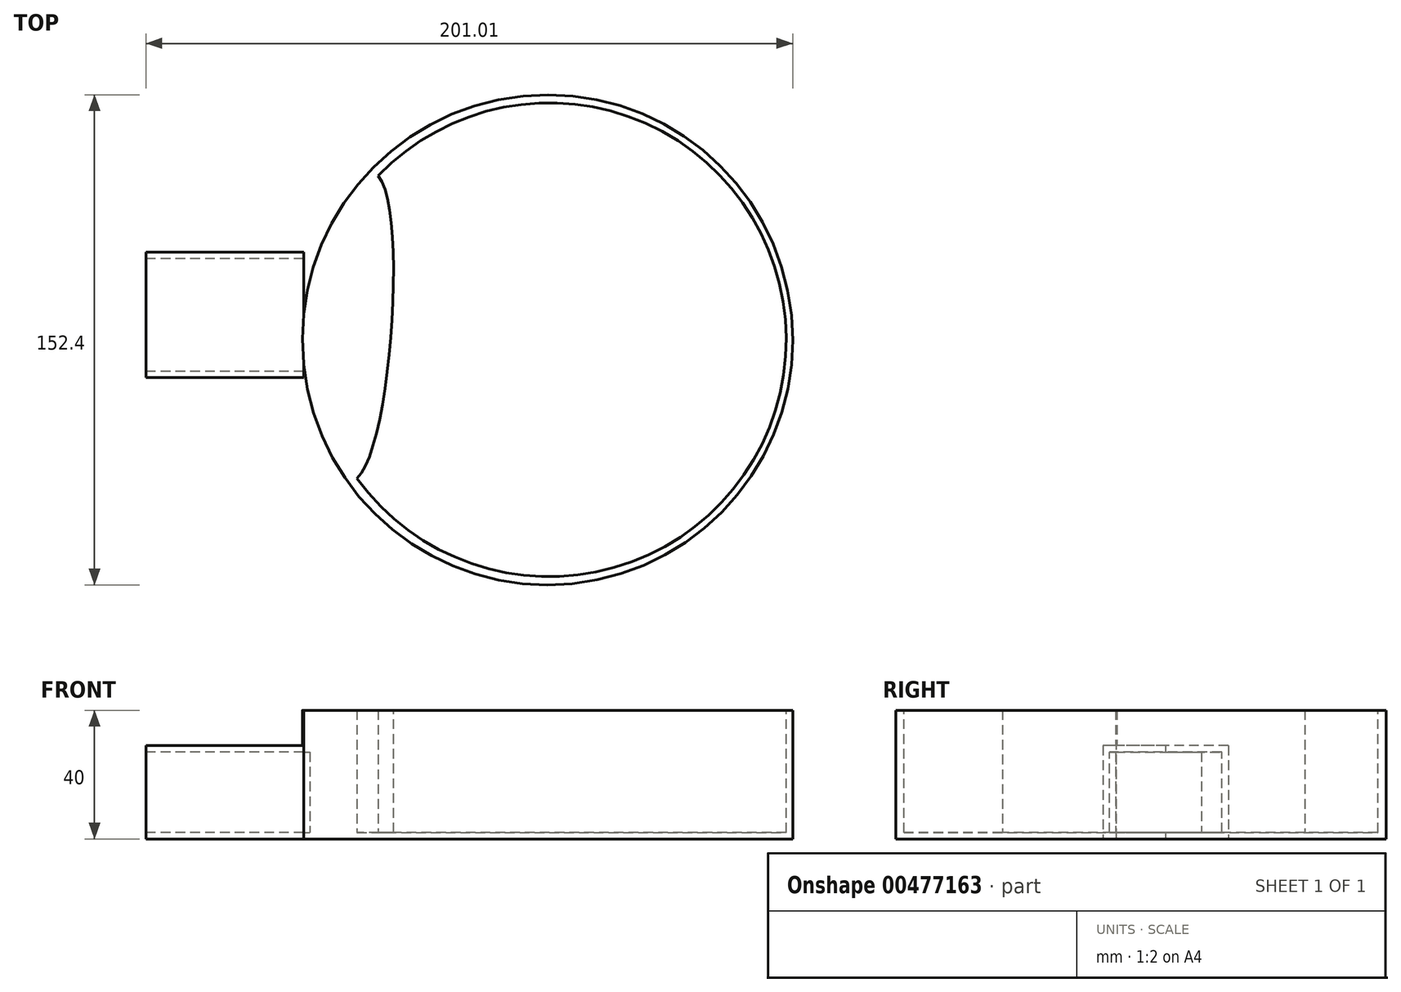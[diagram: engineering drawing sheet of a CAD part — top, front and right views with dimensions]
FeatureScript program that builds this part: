
annotation { "Feature Type Name" : "Feature", "Feature Type Description" : "" }
export const myFeature = defineFeature(function(context is Context, id is Id, definition is map)
    precondition{}
    {
        {
            var Q0;
            Q0=qCreatedBy(makeId("Top.planeOp"),FACE);
            var sketch = newSketch(context, id + "F0", { "sketchPlane" : qUnion([Q0])});
            skLineSegment(sketch, "E0.bottom", {"start": v(-74.8, 22.12) * mm, "end": v(-25.8, 22.12) * mm});
            skLineSegment(sketch, "E0.top", {"start": v(-74.8, -16.88) * mm, "end": v(-25.8, -16.88) * mm});
            skLineSegment(sketch, "E0.left", {"start": v(-74.8, 22.12) * mm, "end": v(-74.8, -16.88) * mm});
            skLineSegment(sketch, "E0.right", {"start": v(-25.8, 22.12) * mm, "end": v(-25.8, -16.88) * mm});
            skPoint(sketch, "E1.firstSnap0", {"position": v(-74.8, 2.62) * mm});
            skPoint(sketch, "E1.oppositeSnap0", {"position": v(-74.8, 2.62) * mm});
            skSolve(sketch);
        }
        {
            var Q0;
            Q0=makeQuery(id+"F0.imprint","IMPRINT",FACE,{"disambiguationData":[TD([[makeQuery(id+"F0.imprint","IMPRINT",EDGE,{"derivedFrom":sQuery(id+"F0.wireOp",EDGE,"E0.bottom")}),-1.0]])]});
            extrude(context, id + "F1", {"entities" : qUnion([Q0]), "depth" : 29 * mm});
        }
        {
            var Q0;
            Q0=makeQuery(id+"F1.opExtrude","SWEPT_FACE",FACE,{"disambiguationData":[OSD([sQuery(id+"F0.wireOp",EDGE,"E0.left")])]});
            var sketch = newSketch(context, id + "F2", { "sketchPlane" : qUnion([Q0])});
            skLineSegment(sketch, "E2.bottom", {"start": v(-20.12, 27) * mm, "end": v(14.88, 27) * mm});
            skLineSegment(sketch, "E2.top", {"start": v(-20.12, 2) * mm, "end": v(14.88, 2) * mm});
            skLineSegment(sketch, "E2.left", {"start": v(-20.12, 27) * mm, "end": v(-20.12, 2) * mm});
            skLineSegment(sketch, "E2.right", {"start": v(14.88, 27) * mm, "end": v(14.88, 2) * mm});
            skSolve(sketch);
        }
        {
            var Q0;
            Q0=qCreatedBy(makeId("Top.planeOp"),FACE);
            var sketch = newSketch(context, id + "F3", { "sketchPlane" : qUnion([Q0])});
            skCircle(sketch, "E3", {"center": v(50.02, -5.1) * mm, "radius": 76.2 * mm});
            skSolve(sketch);
        }
        {
            var Q0;
            Q0 = qSketchRegion(id + "F3", true);
            extrude(context, id + "F4", {"entities" : qUnion([Q0]), "operationType" : NewBodyOperationType.ADD, "depth" : 40 * mm});
        }
        {
            var Q0;
            Q0=makeQuery(id+"F4.opExtrude","CAP_FACE",FACE,{"disambiguationData":[OSD([sQuery(id+"F3.wireOp",EDGE,"E3")])],"isStart":false});
            var sketch = newSketch(context, id + "F5", { "sketchPlane" : qUnion([Q0])});
            skCircle(sketch, "E4", {"center": v(50.56, -5.1) * mm, "radius": 73.66 * mm});
            skSolve(sketch);
        }
        {
            var Q0;
            Q0 = qSketchRegion(id + "F5", true);
            extrude(context, id + "F6", {"entities" : qUnion([Q0]), "operationType" : NewBodyOperationType.REMOVE, "oppositeDirection" : true, "depth" : 38 * mm});
        }
        {
            var Q0;
            Q0=makeQuery(id+"F2.imprint","IMPRINT",FACE,{"disambiguationData":[TD([[makeQuery(id+"F2.imprint","IMPRINT",EDGE,{"derivedFrom":sQuery(id+"F2.wireOp",EDGE,"E2.bottom")}),-1.0]])]});
            extrude(context, id + "F7", {"entities" : qUnion([Q0]), "operationType" : NewBodyOperationType.REMOVE, "oppositeDirection" : true, "depth" : 147.5 * mm});
        }
        {
            var Q0;
            Q0=makeQuery(id+"F7.boolean.opBoolean","MERGE",FACE,{"derivedFrom":[makeQuery(id+"F6.boolean.opBoolean","COPY",FACE,{"derivedFrom":makeQuery(id+"F6.opExtrude","CAP_FACE",FACE,{"disambiguationData":[OSD([sQuery(id+"F5.wireOp",EDGE,"E4")])],"isStart":false})}),makeQuery(id+"F7.opExtrude","SWEPT_FACE",FACE,{"disambiguationData":[OSD([sQuery(id+"F2.wireOp",EDGE,"E2.top")])]})]});
            var sketch = newSketch(context, id + "F8", { "sketchPlane" : qUnion([Q0])});
            skFitSpline(sketch, "E5", {"points": [v(-9.2, -48.15) * mm, v(-25.8, 0) * mm, v(-2.58, 45.92) * mm, v(-9.2, -48.15) * mm]});
            skSolve(sketch);
        }
        {
            var Q0;
            {var subQ2=sQuery(id+"F2.wireOp",EDGE,"E2.top");var subQ3=makeQuery(id+"F7.opExtrude","SWEPT_FACE",FACE,{"disambiguationData":[OSD([subQ2])]});var subQ5=sQuery(id+"F3.wireOp",EDGE,"E3");var subQ6=makeQuery(id+"F4.opExtrude","SWEPT_FACE",FACE,{"disambiguationData":[OSD([subQ5])]});var subQ21=subQ6;var subQ24=makeQuery(id+"F7.boolean.opBoolean","INTERSECT",EDGE,{"disambiguationData":[OD(1.0)],"derivedFrom":[subQ21,subQ3]});Q0=makeQuery(id+"F8.imprint","IMPRINT",FACE,{"disambiguationData":[TD([[makeQuery(id+"F8.imprint","IMPRINT",EDGE,{"derivedFrom":subQ24}),-1.0]])]});}
            extrude(context, id + "F9", {"entities" : qUnion([Q0]), "operationType" : NewBodyOperationType.ADD, "depth" : 38 * mm});
        }
    });
